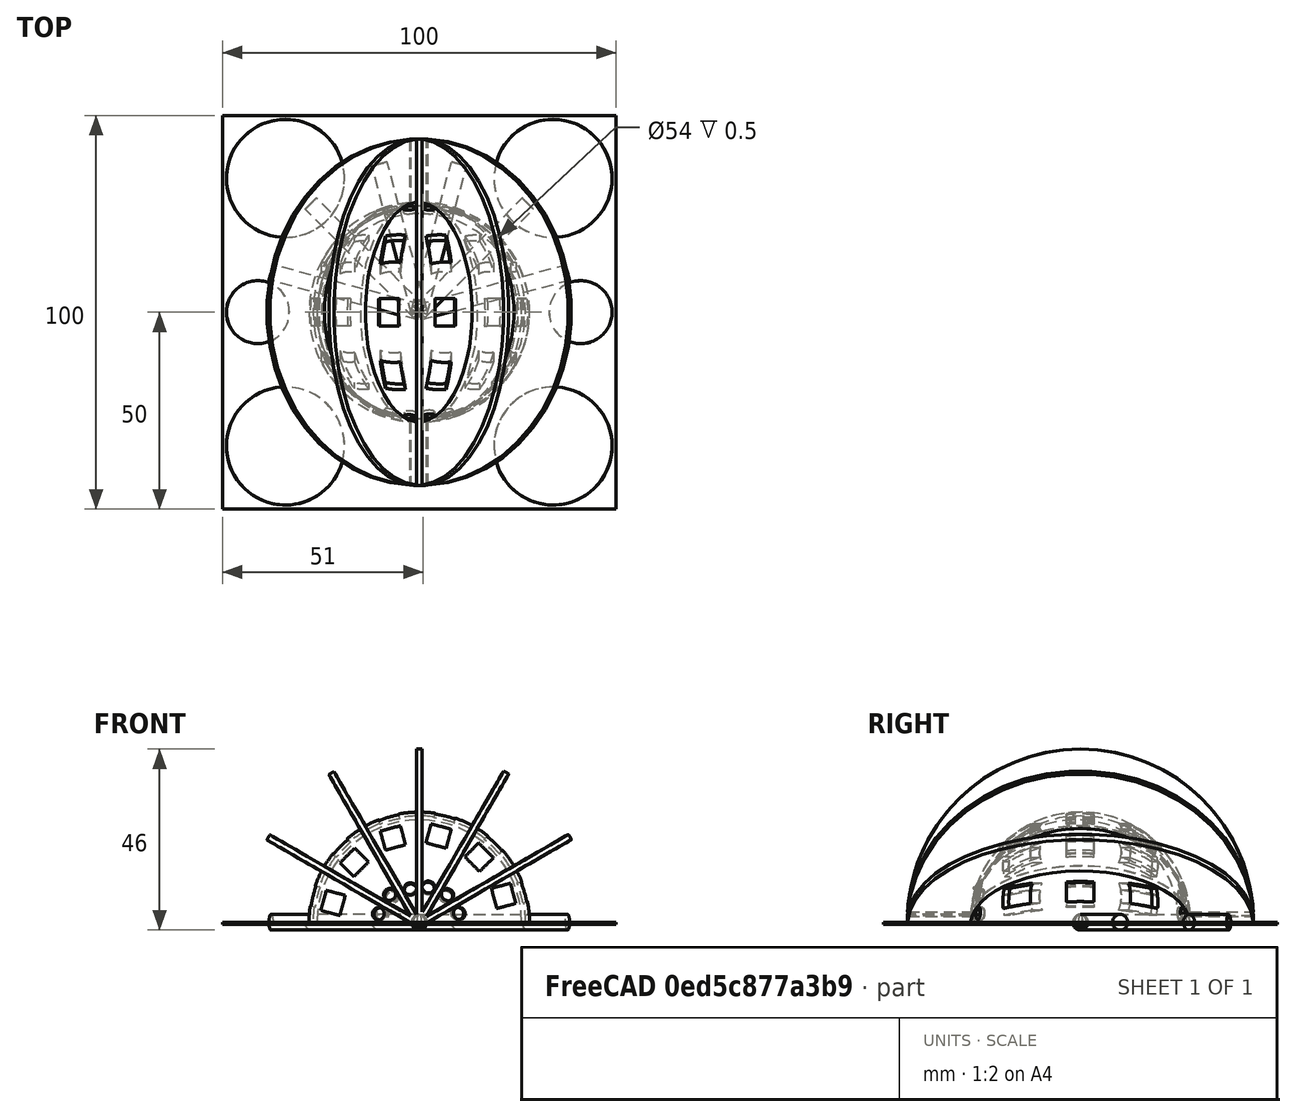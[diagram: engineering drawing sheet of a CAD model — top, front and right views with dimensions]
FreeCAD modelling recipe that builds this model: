
FCSTD DOCUMENT  (FreeCAD 0.16R6703 (Git))
Label: Led_support_v28b_rotado
Comment: Version 1.5\nEsfera exterior 40mm\nEsfera interior 25mm\n\nVersion 2.3\nEsfera exterior  48mm\nEsfera interior  32mm\n\n\nVersion 2.5\nEsfera exterior  44mm\nEsfera interior  28mm mal.. lo dewje en 32... (+106 chars)
License: CreativeCommons Attribution-ShareAlike
LicenseURL: http://creativecommons.org/licenses/by-sa/4.0/
objects: Part::Cylinder×14, Part::Sphere×10, Part::Box×10, Part::Cut×9, Part::MultiFuse×5, Part::FeaturePython×4
note: 52 computed .brp shape members not serialized (recipe doc carries the construction recipe); baked Part::Feature solids carry a one-line shape summary decoded from their .brp

FEATURE [Part::Sphere] Sphere
  Angle1 = -90
  Angle2 = 90
  Angle3 = 180
  Radius = 44
FEATURE [Part::Box] Box  label="Cube"
  Height = 100
  Length = 1.5
  Placement = pos=(-0.75,0,-50) rot=(0,0,1;0rad)
  Width = 50
FEATURE [Part::Box] Box001  label="Cube001"
  Height = 100
  Length = 1.5
  Placement = pos=(-0.75,0,-50) rot=(0,0,-1;0.523599rad)
  Width = 50
FEATURE [Part::Box] Box002  label="Cube002"
  Height = 100
  Length = 1.5
  Placement = pos=(-0.75,0,-50) rot=(0,0,-1;1.0472rad)
  Width = 50
FEATURE [Part::Box] Box003  label="Cube003"
  Height = 100
  Length = 0.5
  Placement = pos=(0,0,-50) rot=(0,0,-1;1.5708rad)
  Width = 50
FEATURE [Part::Box] Box004  label="Cube004"
  Height = 100
  Length = 1.5
  Placement = pos=(-0.75,-1,-50) rot=(0,0,1;0.523599rad)
  Width = 50
FEATURE [Part::Sphere] Sphere001
  Angle1 = -90
  Angle2 = 90
  Angle3 = 180
  Radius = 28
FEATURE [Part::Sphere] Sphere002
  Angle1 = -90
  Angle2 = 90
  Angle3 = 180
  Radius = 100
FEATURE [Part::Cut] Cut
  Base = -> Sphere002
  Tool = -> Sphere
FEATURE [Part::Box] Box005  label="Cube005"
  Height = 100
  Length = 1.5
  Placement = pos=(-0.75,-1,-50) rot=(0,0,1;1.0472rad)
  Width = 50
FEATURE [Part::Box] Box006  label="Cube006"
  Height = 100
  Length = 0.5
  Placement = pos=(0,-0.5,-50) rot=(0,0,1;1.5708rad)
  Width = 50
FEATURE [Part::MultiFuse] Fusion
  Shapes = -> [Box,Box001,Box002,Box003,Box004,Box005,Box006]
FEATURE [Part::Cut] Cut001
  Base = -> Fusion
  Tool = -> Cut
FEATURE [Part::Sphere] Sphere003
  Angle1 = -90
  Angle2 = 90
  Angle3 = 180
  Radius = 27
FEATURE [Part::Cylinder] Cylinder
  Angle = 360
  Height = 39
  Placement = pos=(0,0,0) rot=(-0.129428,0.983106,0.129428;1.58783rad)
  Radius = 2
FEATURE [Part::FeaturePython] Array  # Draft array (typed FeaturePython)
  Angle = 150
  ArrayType = 1
  Axis = (0,0,1)
  Base = -> Cylinder
  Center = (0,0,0)
  Fuse = false
  IntervalAxis = (0,0,0)
  IntervalX = (1,0,0)
  IntervalY = (0,1,0)
  IntervalZ = (0,0,0)
  NumberPolar = 6
  NumberX = 2
  NumberY = 2
  NumberZ = 1
FEATURE [Part::Box] Box007  label="aplanar"
  Height = 100
  Length = 2.5
  Placement = pos=(50.5,-3,-50) rot=(0,0,1;1.5708rad)
  Width = 100
FEATURE [Part::Cylinder] Cylinder001
  Angle = 360
  Height = 39
  Placement = pos=(0,0,0) rot=(-0.854278,-0.301553,-0.423408;0.353759rad)
  Radius = 1.6
FEATURE [Part::Cylinder] Cylinder002
  Angle = 360
  Height = 39
  Placement = pos=(0,0,0) rot=(-0.869339,0.295158,0.396398;0.367291rad)
  Radius = 1.6
FEATURE [Part::Cylinder] Cylinder003
  Angle = 360
  Height = 39
  Placement = pos=(0,0,0) rot=(-0.616167,0.461037,-0.638579;0.478391rad)
  Radius = 1.6
FEATURE [Part::Cylinder] Cylinder004
  Angle = 360
  Height = 39
  Placement = pos=(0,0,0) rot=(-0.540302,-0.361344,0.759937;0.587001rad)
  Radius = 1.6
FEATURE [Part::Cylinder] Cylinder005
  Angle = 360
  Height = 39
  Placement = pos=(0,0,0) rot=(-0.234249,-0.208821,0.949485;1.32751rad)
  Radius = 1.6
FEATURE [Part::Cylinder] Cylinder006
  Angle = 360
  Height = 39
  Placement = pos=(0,0,0) rot=(-0.231467,0.19131,-0.953847;1.36645rad)
  Radius = 1.6
FEATURE [Part::Cylinder] Cylinder007
  Angle = 360
  Height = 39
  Placement = pos=(0,0,0) rot=(0.99,0.139135,-0.023283;3.46995rad)
  Radius = 1.6
FEATURE [Part::Cylinder] Cylinder008
  Angle = 360
  Height = 39
  Placement = pos=(0,0,0) rot=(0.991208,-0.130495,0.021837;3.47034rad)
  Radius = 1.6
FEATURE [Part::Cylinder] Cylinder009
  Angle = 360
  Height = 39
  Placement = pos=(0,0,0) rot=(0.991881,-0.000477,0.12717;3.3856rad)
  Radius = 1.6
FEATURE [Part::Cylinder] Cylinder010
  Angle = 360
  Height = 39
  Placement = pos=(0,0,0) rot=(0.665173,0.746686,0.001947;3.49198rad)
  Radius = 1.6
FEATURE [Part::Cylinder] Cylinder011
  Angle = 360
  Height = 39
  Placement = pos=(0,0,0) rot=(0.632288,0.770157,-0.084087;3.46155rad)
  Radius = 1.6
FEATURE [Part::Cylinder] Cylinder012
  Angle = 360
  Height = 39
  Placement = pos=(0,0,0) rot=(-0.512551,0.856651,-0.058661;2.78614rad)
  Radius = 1.6
FEATURE [Part::MultiFuse] Fusion002
  Shapes = -> [Cylinder001,Cylinder002,Cylinder003,Cylinder004,Cylinder005,Cylinder006,Cylinder007,Cylinder008,Cylinder009,Cylinder010,Cylinder011,Cylinder012]
FEATURE [Part::Sphere] Sphere004
  Angle1 = -90
  Angle2 = 90
  Angle3 = 360
  Placement = pos=(-34,0,-34) rot=(0,0,1;0rad)
  Radius = 15
FEATURE [Part::Sphere] Sphere005
  Angle1 = -90
  Angle2 = 90
  Angle3 = 360
  Placement = pos=(34,0,-34) rot=(0,0,1;0rad)
  Radius = 15
FEATURE [Part::Sphere] Sphere006
  Angle1 = -90
  Angle2 = 90
  Angle3 = 360
  Placement = pos=(34,0,34) rot=(0,0,1;0rad)
  Radius = 15
FEATURE [Part::Sphere] Sphere007
  Angle1 = -90
  Angle2 = 90
  Angle3 = 360
  Placement = pos=(-34,0,34) rot=(0,0,1;0rad)
  Radius = 15
FEATURE [Part::MultiFuse] Fusion003
  Shapes = -> [Sphere004,Sphere005,Sphere006,Sphere007]
FEATURE [Part::Sphere] Sphere008
  Angle1 = -90
  Angle2 = 90
  Angle3 = 360
  Placement = pos=(41,0,0) rot=(0,0,1;0rad)
  Radius = 8
FEATURE [Part::FeaturePython] Array001  # Draft array (typed FeaturePython)
  Angle = 360
  ArrayType = 1
  Axis = (0,0,1)
  Base = -> Sphere008
  Center = (0,0,0)
  Fuse = false
  IntervalAxis = (0,0,0)
  IntervalX = (0,0,0)
  IntervalY = (0,0,0)
  IntervalZ = (0,0,0)
  NumberPolar = 2
  NumberX = 2
  NumberY = 2
  NumberZ = 1
  Placement = pos=(0,0,0) rot=(1,0,0;1.5708rad)
FEATURE [Part::Sphere] Sphere009
  Angle1 = -90
  Angle2 = 90
  Angle3 = 180
  Placement = pos=(0,-1,0) rot=(1,0,0;1.5708rad)
  Radius = 26
FEATURE [Part::Box] Box008  label="Cubo"
  Height = 120
  Length = 5
  Placement = pos=(-25,3,-60) rot=(0,0,-1;0.261799rad)
  Width = 5.3
FEATURE [Part::FeaturePython] Array002  # Draft array (typed FeaturePython)
  Angle = 360
  ArrayType = 1
  Axis = (0,0,1)
  Base = -> Box008
  Center = (0,0,0)
  Fuse = false
  IntervalAxis = (0,0,0)
  IntervalX = (1,0,0)
  IntervalY = (0,1,0)
  IntervalZ = (0,0,0)
  NumberPolar = 12
  NumberX = 2
  NumberY = 2
  NumberZ = 1
FEATURE [Part::Box] Box009  label="Cubo001"
  Height = 7
  Length = 5.3
  Placement = pos=(-2.65,-2.65,-3.5) rot=(0,0,1;0.261799rad)
  Width = 60
FEATURE [Part::FeaturePython] Array003  # Draft array (typed FeaturePython)
  Angle = 360
  ArrayType = 1
  Axis = (0,0,1)
  Base = -> Box009
  Center = (0,0,0)
  Fuse = false
  IntervalAxis = (0,0,0)
  IntervalX = (1,0,0)
  IntervalY = (0,1,0)
  IntervalZ = (0,0,0)
  NumberPolar = 12
  NumberX = 2
  NumberY = 2
  NumberZ = 1
FEATURE [Part::MultiFuse] Fusion001
  Shapes = -> [Sphere001,Cut001]
FEATURE [Part::Cut] Cut002
  Base = -> Fusion001
  Tool = -> Sphere003
FEATURE [Part::Cut] Cut003
  Base = -> Cut002
  Tool = -> Fusion002
FEATURE [Part::Cut] Cut004
  Base = -> Cut003
  Tool = -> Fusion003
FEATURE [Part::Cylinder] Cylinder013
  Angle = 360
  Height = 10
  Placement = pos=(1,0,0) rot=(1,0,0;1.5708rad)
  Radius = 27
FEATURE [Part::Cut] Cut005
  Base = -> Cut004
  Tool = -> Cylinder013
FEATURE [Part::MultiFuse] Fusion004  label="agujeros de led"
  Shapes = -> [Array002,Array003]
FEATURE [Part::Cut] Cut006
  Base = -> Cut005
  Tool = -> Fusion004
FEATURE [Part::Cut] Cut007
  Base = -> Cut006
  Tool = -> Array001
FEATURE [Part::Cut] Cut008
  Base = -> Cut007
  Placement = pos=(0,0,0) rot=(1,0,0;1.5708rad)
  Tool = -> Box007
